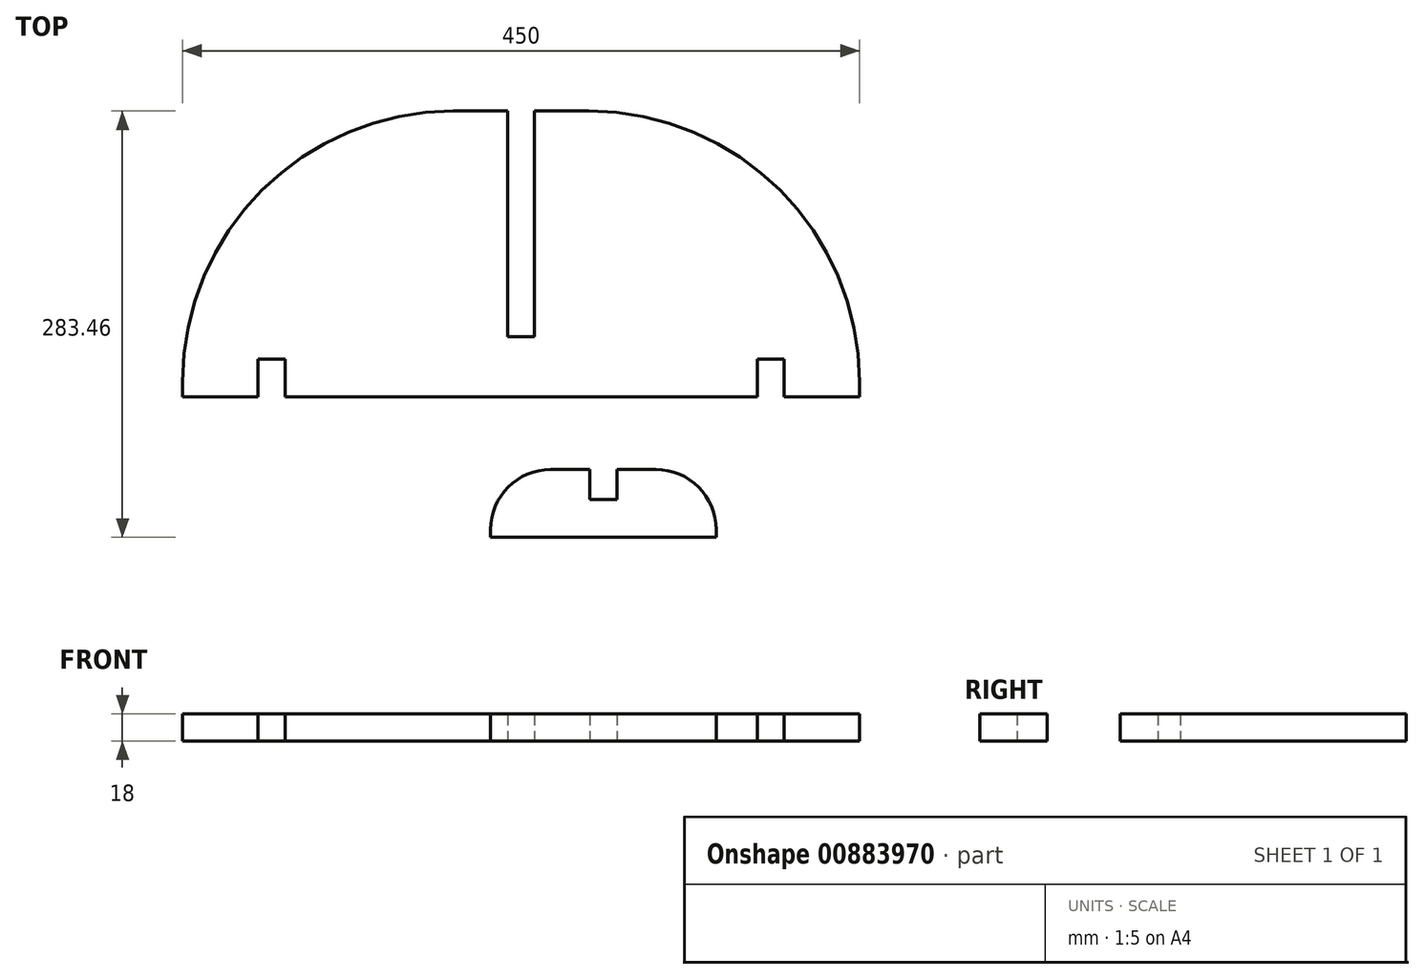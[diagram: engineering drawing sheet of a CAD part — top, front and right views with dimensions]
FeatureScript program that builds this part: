
annotation { "Feature Type Name" : "Feature", "Feature Type Description" : "" }
export const myFeature = defineFeature(function(context is Context, id is Id, definition is map)
    precondition{}
    {
        {
            var Q0;
            Q0=qCreatedBy(makeId("Top.planeOp"),FACE);
            var sketch = newSketch(context, id + "F0", { "sketchPlane" : qUnion([Q0])});
            skLineSegment(sketch, "E0", {"start": v(-225, 0) * mm, "end": v(225, 0) * mm});
            skLineSegment(sketch, "E1", {"start": v(225, 0) * mm, "end": v(225, 10) * mm});
            skLineSegment(sketch, "E2", {"start": v(-225, 0) * mm, "end": v(-225, 10) * mm});
            skLineSegment(sketch, "E3", {"start": v(-9, 186.36) * mm, "end": v(-9, 40) * mm});
            skLineSegment(sketch, "E4", {"start": v(-9, 40) * mm, "end": v(9, 40) * mm});
            skLineSegment(sketch, "E5", {"start": v(9, 40) * mm, "end": v(9, 186.36) * mm});
            skArc(sketch, "E6", {"start": v(-45, 190) * mm, "mid": v(-172.28, 137.28) * mm, "end": v(-225, 10) * mm});
            skArc(sketch, "E7", {"start": v(225, 10) * mm, "mid": v(172.28, 137.28) * mm, "end": v(45, 190) * mm});
            skLineSegment(sketch, "E8", {"start": v(0, 0) * mm, "end": v(0, 40) * mm, "construction": true});
            skLineSegment(sketch, "E9", {"start": v(-45, 190) * mm, "end": v(-9, 190) * mm});
            skLineSegment(sketch, "E10", {"start": v(-9, 190) * mm, "end": v(-9, 186.36) * mm});
            skLineSegment(sketch, "E11", {"start": v(9, 186.36) * mm, "end": v(9, 190) * mm});
            skLineSegment(sketch, "E12", {"start": v(9, 190) * mm, "end": v(45, 190) * mm});
            skLineSegment(sketch, "E13", {"start": v(-175, 0) * mm, "end": v(-175, 25) * mm});
            skLineSegment(sketch, "E14", {"start": v(-175, 25) * mm, "end": v(-157, 25) * mm});
            skLineSegment(sketch, "E15", {"start": v(-157, 25) * mm, "end": v(-157, 0) * mm});
            skLineSegment(sketch, "E16", {"start": v(157, 0) * mm, "end": v(157, 25) * mm});
            skLineSegment(sketch, "E17", {"start": v(157, 25) * mm, "end": v(175, 25) * mm});
            skLineSegment(sketch, "E18", {"start": v(175, 25) * mm, "end": v(175, 0) * mm});
            skSolve(sketch);
        }
        {
            var Q0;
            {var subQ3=sQuery(id+"F0.wireOp",EDGE,"E1");Q0=makeQuery(id+"F0.imprint","IMPRINT",FACE,{"disambiguationData":[TD([[makeQuery(id+"F0.imprint","IMPRINT",EDGE,{"derivedFrom":subQ3}),1.0]])]});}
            extrude(context, id + "F1", {"entities" : qUnion([Q0]), "depth" : 18 * mm, "offsetDistance" : 25 * mm});
        }
        {
            var Q0;
            Q0=qCreatedBy(makeId("Top.planeOp"),FACE);
            var sketch = newSketch(context, id + "F2", { "sketchPlane" : qUnion([Q0])});
            skLineSegment(sketch, "E19", {"start": v(129.68, -93.46) * mm, "end": v(-20.32, -93.46) * mm});
            skLineSegment(sketch, "E20", {"start": v(-20.32, -93.46) * mm, "end": v(-20.32, -88.46) * mm});
            skLineSegment(sketch, "E21", {"start": v(19.68, -48.46) * mm, "end": v(45.68, -48.46) * mm});
            skLineSegment(sketch, "E22", {"start": v(45.68, -48.46) * mm, "end": v(45.68, -68.46) * mm});
            skLineSegment(sketch, "E23", {"start": v(45.68, -68.46) * mm, "end": v(63.68, -68.46) * mm});
            skLineSegment(sketch, "E24", {"start": v(63.68, -68.46) * mm, "end": v(63.68, -48.46) * mm});
            skLineSegment(sketch, "E25", {"start": v(63.68, -48.46) * mm, "end": v(89.68, -48.46) * mm});
            skLineSegment(sketch, "E26", {"start": v(129.68, -93.46) * mm, "end": v(129.68, -88.46) * mm});
            skArc(sketch, "E27", {"start": v(19.68, -48.46) * mm, "mid": v(-8.6, -60.18) * mm, "end": v(-20.32, -88.46) * mm});
            skArc(sketch, "E28", {"start": v(129.68, -88.46) * mm, "mid": v(117.97, -60.18) * mm, "end": v(89.68, -48.46) * mm});
            skLineSegment(sketch, "E29", {"start": v(54.68, -68.46) * mm, "end": v(54.68, -93.46) * mm, "construction": true});
            skSolve(sketch);
        }
        {
            var Q0;
            Q0=makeQuery(id+"F2.imprint","IMPRINT",FACE,{"disambiguationData":[TD([[makeQuery(id+"F2.imprint","IMPRINT",EDGE,{"derivedFrom":sQuery(id+"F2.wireOp",EDGE,"E19")}),-1.0]])]});
            extrude(context, id + "F3", {"entities" : qUnion([Q0]), "depth" : 18 * mm, "offsetDistance" : 25 * mm});
        }
    });
